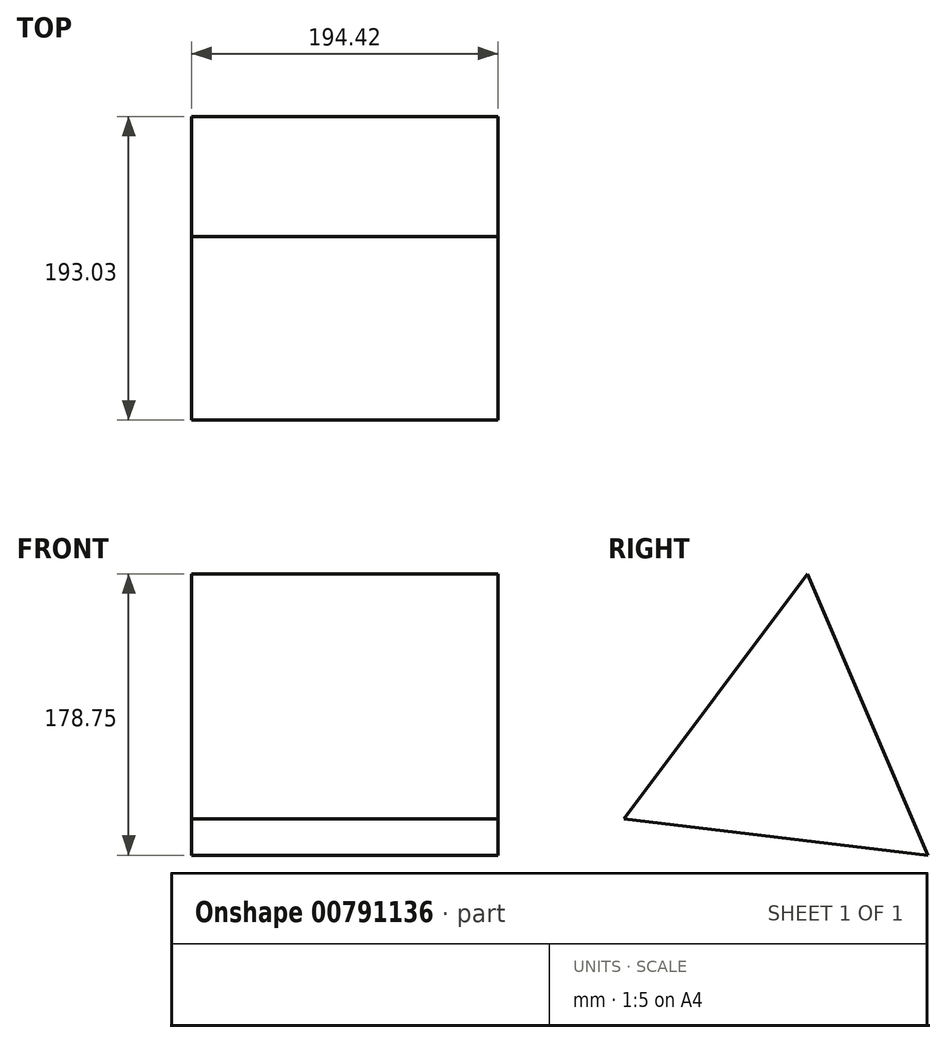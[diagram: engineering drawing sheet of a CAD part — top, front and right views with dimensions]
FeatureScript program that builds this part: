
annotation { "Feature Type Name" : "Feature", "Feature Type Description" : "" }
export const myFeature = defineFeature(function(context is Context, id is Id, definition is map)
    precondition{}
    {
        {
            var Q0;
            Q0=qCreatedBy(makeId("Right.planeOp"),FACE);
            var sketch = newSketch(context, id + "F0", { "sketchPlane" : qUnion([Q0])});
            skCircle(sketch, "E0.cCircle", {"center": v(-351.06, 95.25) * mm, "radius": 56.12 * mm, "construction": true});
            skLineSegment(sketch, "E0.0", {"start": v(-261.23, 27.95) * mm, "end": v(-454.26, 51.1) * mm});
            skLineSegment(sketch, "E0.1", {"start": v(-454.26, 51.1) * mm, "end": v(-337.7, 206.7) * mm});
            skLineSegment(sketch, "E0.2", {"start": v(-337.7, 206.7) * mm, "end": v(-261.23, 27.95) * mm});
            skPoint(sketch, "E0.0.midPoint", {"position": v(-357.74, 39.53) * mm});
            skLineSegment(sketch, "E1", {"start": v(-351.06, 95.25) * mm, "end": v(0, 0) * mm, "construction": true});
            skSolve(sketch);
        }
        {
            var Q0;
            Q0 = qSketchRegion(id + "F0", true);
            extrude(context, id + "F1", {"entities" : qUnion([Q0]), "depth" : 194.42 * mm, "offsetDistance" : 25.4 * mm});
        }
    });
